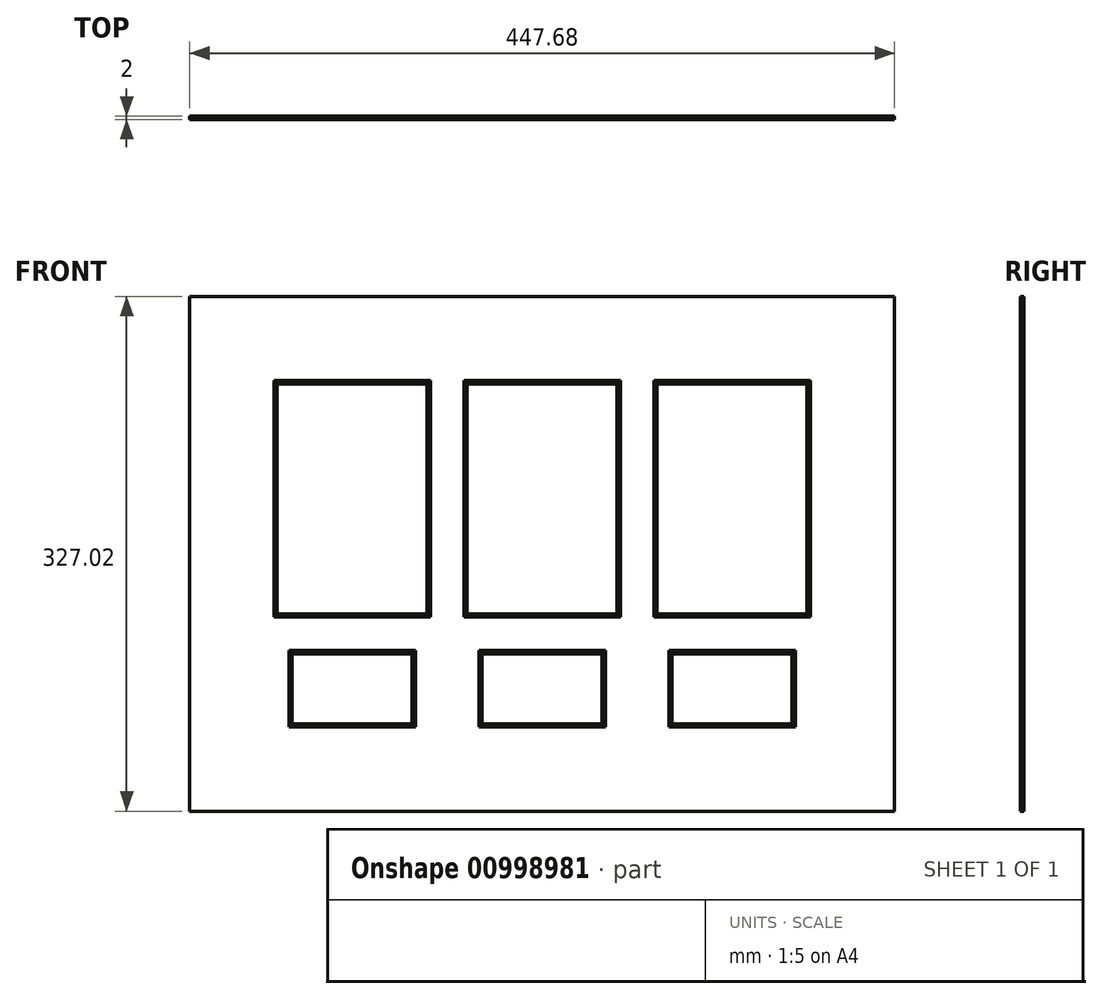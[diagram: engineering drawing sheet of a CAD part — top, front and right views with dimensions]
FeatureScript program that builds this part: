
annotation { "Feature Type Name" : "Feature", "Feature Type Description" : "" }
export const myFeature = defineFeature(function(context is Context, id is Id, definition is map)
    precondition{}
    {
        {
            var Q0;
            Q0=qCreatedBy(makeId("Front.planeOp"),FACE);
            var sketch = newSketch(context, id + "F0", { "sketchPlane" : qUnion([Q0])});
            skLineSegment(sketch, "E0.bottom", {"start": v(223.84, -163.51) * mm, "end": v(-223.84, -163.51) * mm});
            skLineSegment(sketch, "E0.top", {"start": v(223.84, 163.51) * mm, "end": v(-223.84, 163.51) * mm});
            skLineSegment(sketch, "E0.left", {"start": v(223.84, -163.51) * mm, "end": v(223.84, 163.51) * mm});
            skLineSegment(sketch, "E0.right", {"start": v(-223.84, -163.51) * mm, "end": v(-223.84, 163.51) * mm});
            skPoint(sketch, "E0.middle", {"position": v(0, 0) * mm});
            skLineSegment(sketch, "E1.bottom", {"start": v(-168.28, 107.95) * mm, "end": v(-73.03, 107.95) * mm});
            skLineSegment(sketch, "E1.top", {"start": v(-168.28, -38.1) * mm, "end": v(-73.03, -38.1) * mm});
            skLineSegment(sketch, "E1.left", {"start": v(-168.28, 107.95) * mm, "end": v(-168.28, -38.1) * mm});
            skLineSegment(sketch, "E1.right", {"start": v(-73.03, 107.95) * mm, "end": v(-73.03, -38.1) * mm});
            skLineSegment(sketch, "E2.MirrorCS", {"start": v(168.28, -38.1) * mm, "end": v(73.03, -38.1) * mm});
            skLineSegment(sketch, "E3.bottom", {"start": v(-47.62, -38.1) * mm, "end": v(47.63, -38.1) * mm});
            skLineSegment(sketch, "E3.top", {"start": v(-47.63, 107.95) * mm, "end": v(47.62, 107.95) * mm});
            skLineSegment(sketch, "E3.left", {"start": v(-47.63, -38.1) * mm, "end": v(-47.63, 107.95) * mm});
            skLineSegment(sketch, "E3.right", {"start": v(47.63, -38.1) * mm, "end": v(47.62, 107.95) * mm});
            skLineSegment(sketch, "E4.bottom", {"start": v(-82.55, -63.5) * mm, "end": v(-158.75, -63.5) * mm});
            skLineSegment(sketch, "E4.top", {"start": v(-82.55, -107.95) * mm, "end": v(-158.75, -107.95) * mm});
            skLineSegment(sketch, "E4.left", {"start": v(-82.55, -63.5) * mm, "end": v(-82.55, -107.95) * mm});
            skLineSegment(sketch, "E4.right", {"start": v(-158.75, -63.5) * mm, "end": v(-158.75, -107.95) * mm});
            skPoint(sketch, "E4.middle", {"position": v(-120.65, -85.73) * mm});
            skPoint(sketch, "E4.middle.positionSnap0", {"position": v(-120.65, -38.1) * mm});
            skPoint(sketch, "E4.centerSnap0", {"position": v(-120.65, -38.1) * mm});
            skLineSegment(sketch, "E5.MirrorCS", {"start": v(82.55, -63.5) * mm, "end": v(82.55, -107.95) * mm});
            skLineSegment(sketch, "E6.MirrorCS", {"start": v(82.55, -63.5) * mm, "end": v(158.75, -63.5) * mm});
            skLineSegment(sketch, "E7.MirrorCS", {"start": v(158.75, -63.5) * mm, "end": v(158.75, -107.95) * mm});
            skLineSegment(sketch, "E8.MirrorCS", {"start": v(82.55, -107.95) * mm, "end": v(158.75, -107.95) * mm});
            skPoint(sketch, "E9.middle", {"position": v(0, -85.73) * mm});
            skLineSegment(sketch, "E10", {"start": v(-260.01, 107.95) * mm, "end": v(263.4, 107.95) * mm, "construction": true});
            skLineSegment(sketch, "E11", {"start": v(73.03, -38.1) * mm, "end": v(73.02, 107.95) * mm});
            skLineSegment(sketch, "E12", {"start": v(168.28, -38.1) * mm, "end": v(168.28, 107.95) * mm});
            skPoint(sketch, "E12.endSnap0", {"position": v(1.7, 107.95) * mm});
            skLineSegment(sketch, "E13", {"start": v(168.28, 107.95) * mm, "end": v(73.03, 107.95) * mm});
            skLineSegment(sketch, "E14.bottom", {"start": v(-38.1, -107.95) * mm, "end": v(38.1, -107.95) * mm});
            skLineSegment(sketch, "E14.top", {"start": v(-38.1, -63.5) * mm, "end": v(38.1, -63.5) * mm});
            skLineSegment(sketch, "E14.left", {"start": v(-38.1, -107.95) * mm, "end": v(-38.1, -63.5) * mm});
            skLineSegment(sketch, "E14.right", {"start": v(38.1, -107.95) * mm, "end": v(38.1, -63.5) * mm});
            skSolve(sketch);
        }
        {
            var Q0;
            Q0=makeQuery(id+"F0.imprint","IMPRINT",FACE,{"disambiguationData":[TD([[makeQuery(id+"F0.imprint","IMPRINT",EDGE,{"derivedFrom":sQuery(id+"F0.wireOp",EDGE,"E0.bottom")}),-1.0]])]});
            extrude(context, id + "F1", {"entities" : qUnion([Q0]), "depth" : 2 * mm, "offsetDistance" : 25.4 * mm});
        }
        {
            var Q0;
            Q0=makeQuery(id+"F1.opExtrude","CAP_EDGE",EDGE,{"disambiguationData":[OSD([sQuery(id+"F0.wireOp",EDGE,"E1.bottom")])],"isStart":false});
            var Q1;
            Q1=makeQuery(id+"F1.opExtrude","CAP_EDGE",EDGE,{"disambiguationData":[OSD([sQuery(id+"F0.wireOp",EDGE,"E1.left")])],"isStart":false});
            var Q2;
            Q2=makeQuery(id+"F1.opExtrude","CAP_EDGE",EDGE,{"disambiguationData":[OSD([sQuery(id+"F0.wireOp",EDGE,"E1.top")])],"isStart":false});
            var Q3;
            Q3=makeQuery(id+"F1.opExtrude","CAP_EDGE",EDGE,{"disambiguationData":[OSD([sQuery(id+"F0.wireOp",EDGE,"E1.right")])],"isStart":false});
            var Q4;
            Q4=makeQuery(id+"F1.opExtrude","CAP_EDGE",EDGE,{"disambiguationData":[OSD([sQuery(id+"F0.wireOp",EDGE,"E3.top")])],"isStart":false});
            var Q5;
            Q5=makeQuery(id+"F1.opExtrude","CAP_EDGE",EDGE,{"disambiguationData":[OSD([sQuery(id+"F0.wireOp",EDGE,"E3.left")])],"isStart":false});
            var Q6;
            Q6=makeQuery(id+"F1.opExtrude","CAP_EDGE",EDGE,{"disambiguationData":[OSD([sQuery(id+"F0.wireOp",EDGE,"E3.right")])],"isStart":false});
            var Q7;
            Q7=makeQuery(id+"F1.opExtrude","CAP_EDGE",EDGE,{"disambiguationData":[OSD([sQuery(id+"F0.wireOp",EDGE,"E3.bottom")])],"isStart":false});
            var Q8;
            Q8=makeQuery(id+"F1.opExtrude","CAP_EDGE",EDGE,{"disambiguationData":[OSD([sQuery(id+"F0.wireOp",EDGE,"E2.MirrorCS")])],"isStart":false});
            var Q9;
            Q9=makeQuery(id+"F1.opExtrude","CAP_EDGE",EDGE,{"disambiguationData":[OSD([sQuery(id+"F0.wireOp",EDGE,"E11")])],"isStart":false});
            var Q10;
            Q10=makeQuery(id+"F1.opExtrude","CAP_EDGE",EDGE,{"disambiguationData":[OSD([sQuery(id+"F0.wireOp",EDGE,"E12")])],"isStart":false});
            var Q11;
            Q11=makeQuery(id+"F1.opExtrude","CAP_EDGE",EDGE,{"disambiguationData":[OSD([sQuery(id+"F0.wireOp",EDGE,"E13")])],"isStart":false});
            var Q12;
            Q12=makeQuery(id+"F1.opExtrude","CAP_EDGE",EDGE,{"disambiguationData":[OSD([sQuery(id+"F0.wireOp",EDGE,"E6.MirrorCS")])],"isStart":false});
            var Q13;
            Q13=makeQuery(id+"F1.opExtrude","CAP_EDGE",EDGE,{"disambiguationData":[OSD([sQuery(id+"F0.wireOp",EDGE,"E8.MirrorCS")])],"isStart":false});
            var Q14;
            Q14=makeQuery(id+"F1.opExtrude","CAP_EDGE",EDGE,{"disambiguationData":[OSD([sQuery(id+"F0.wireOp",EDGE,"E7.MirrorCS")])],"isStart":false});
            var Q15;
            Q15=makeQuery(id+"F1.opExtrude","CAP_EDGE",EDGE,{"disambiguationData":[OSD([sQuery(id+"F0.wireOp",EDGE,"E5.MirrorCS")])],"isStart":false});
            var Q16;
            Q16=makeQuery(id+"F1.opExtrude","CAP_EDGE",EDGE,{"disambiguationData":[OSD([sQuery(id+"F0.wireOp",EDGE,"E14.right")])],"isStart":false});
            var Q17;
            Q17=makeQuery(id+"F1.opExtrude","CAP_EDGE",EDGE,{"disambiguationData":[OSD([sQuery(id+"F0.wireOp",EDGE,"E14.top")])],"isStart":false});
            var Q18;
            Q18=makeQuery(id+"F1.opExtrude","CAP_EDGE",EDGE,{"disambiguationData":[OSD([sQuery(id+"F0.wireOp",EDGE,"E14.left")])],"isStart":false});
            var Q19;
            Q19=makeQuery(id+"F1.opExtrude","CAP_EDGE",EDGE,{"disambiguationData":[OSD([sQuery(id+"F0.wireOp",EDGE,"E14.bottom")])],"isStart":false});
            var Q20;
            Q20=makeQuery(id+"F1.opExtrude","CAP_EDGE",EDGE,{"disambiguationData":[OSD([sQuery(id+"F0.wireOp",EDGE,"E4.top")])],"isStart":false});
            var Q21;
            Q21=makeQuery(id+"F1.opExtrude","CAP_EDGE",EDGE,{"disambiguationData":[OSD([sQuery(id+"F0.wireOp",EDGE,"E4.left")])],"isStart":false});
            var Q22;
            Q22=makeQuery(id+"F1.opExtrude","CAP_EDGE",EDGE,{"disambiguationData":[OSD([sQuery(id+"F0.wireOp",EDGE,"E4.bottom")])],"isStart":false});
            var Q23;
            Q23=makeQuery(id+"F1.opExtrude","CAP_EDGE",EDGE,{"disambiguationData":[OSD([sQuery(id+"F0.wireOp",EDGE,"E4.right")])],"isStart":false});
            chamfer(context, id + "F2", {"entities" : qUnion([Q0, Q1, Q2, Q3, Q4, Q5, Q6, Q7, Q8, Q9, Q10, Q11, Q12, Q13, Q14, Q15, Q16, Q17, Q18, Q19, Q20, Q21, Q22, Q23]), "chamferType" : ChamferType.OFFSET_ANGLE, "width" : 2.03 * mm, "oppositeDirection" : false, "angle" : 45 * degree, "tangentPropagation" : true});
        }
    });
